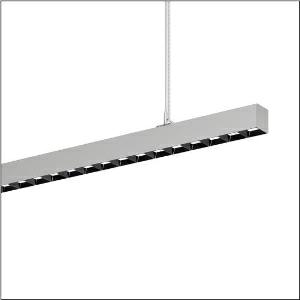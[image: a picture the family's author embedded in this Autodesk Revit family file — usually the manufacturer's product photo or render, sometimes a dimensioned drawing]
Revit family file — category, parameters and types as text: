
# Revit family: silica_r__21_51mx32dc4dsb_d767
name_source: partatom
category: Lighting Fixtures
units: mm (PartAtom-declared; Revit-internal decimal feet)

## family parameters
Cut with Voids When Loaded = No
Host = Face
Light Source = No
Part Type = Normal
Room Calculation Point = No
Round Connector Dimension = Use Diameter
Shared = No

## types (1)
- --- (1 x LED, 18230 lm, 105.8 W, 4000K)
    Apparent Load = 106 VA
    CIE Flux Codes = 86 99 100 59 100
    Color Rendering = 80
    Color Temperature = 4000K
    Default Elevation = 1800 mm
    Description = Silica® 21, office luminaire, primary light control with darklight reflector, of PMMA, black, CAT 2 (L<= 3000cd/m²), light emission: direct/indirect distribution, primary light characteristic: symmetric, installation type: suspended mounting, LED, rated luminous flux: 18.230lm, luminous efficacy: 172lm/W, light colour: 840, colour temperature: 4000K, with terminal, 3+2-pole, max. 2.5mm², mains connection: 220..240V, AC, 50/60Hz, rated input power: 105.8W, luminaire housing, of aluminium, metallic grey (RAL 9006), length: 3.004mm, width: 53mm, height: 53mm, protection rating (complete): IP20, insulation class (complete): insulation class I (protective earthing), certification: CE, permissible operating ambient temperature: 0..+35°C, standard: EN 50419, packaging unit: 1 piece
    Height = 53 mm
    Lamp = 1 x LED
    Lamp Light Flux = 18230 lm
    Lamp Power = 105.8 W
    Lamp count = 1
    Length = 3004 mm
    Luminous efficacy = 172 lm/W
    Manufacturer = Siteco
    ModVariant = No
    Model = 51MX32DC4DSB
    Mounting Place = Ceiling
    Mounting Type = Pendant
    Number of Poles = 1
    OnlyDefault = Yes
    Power Factor = 1
    Product Name = Silica® 21
    Product group = office luminaire | ceiling pendant
    ProductGroupID = 902
    Protection Class = Protection class I
    Protection Degree = IP 20
    RLX_Detail_Level = 1
    RLX_Emergency_Light_Flux = 0 lm
    RLX_Emergency_Type = 0
    RLX_Emergency_Type_DB = No
    RlxData = <blob elided: 67165 chars, md5=df0143d2>
    Socket = socket
    Standby Power = 0 W
    System Light Flux = 18230 lm
    System Power = 106 W
    Type Comments = factory setting: luminous flux: 100 % | dim-lin: 254 | 366 mA
    Type Image = l_1297751.jpg
    URL = http://relux.com
    VarID = @adj_052679
    Voltage = 0 V
    Weight = 0.00 kg
    Width = 53 mm

## geometry (parser evidence)
native form markers: Blend x4, Sweep x11
no freeform markers — native parametric forms only
